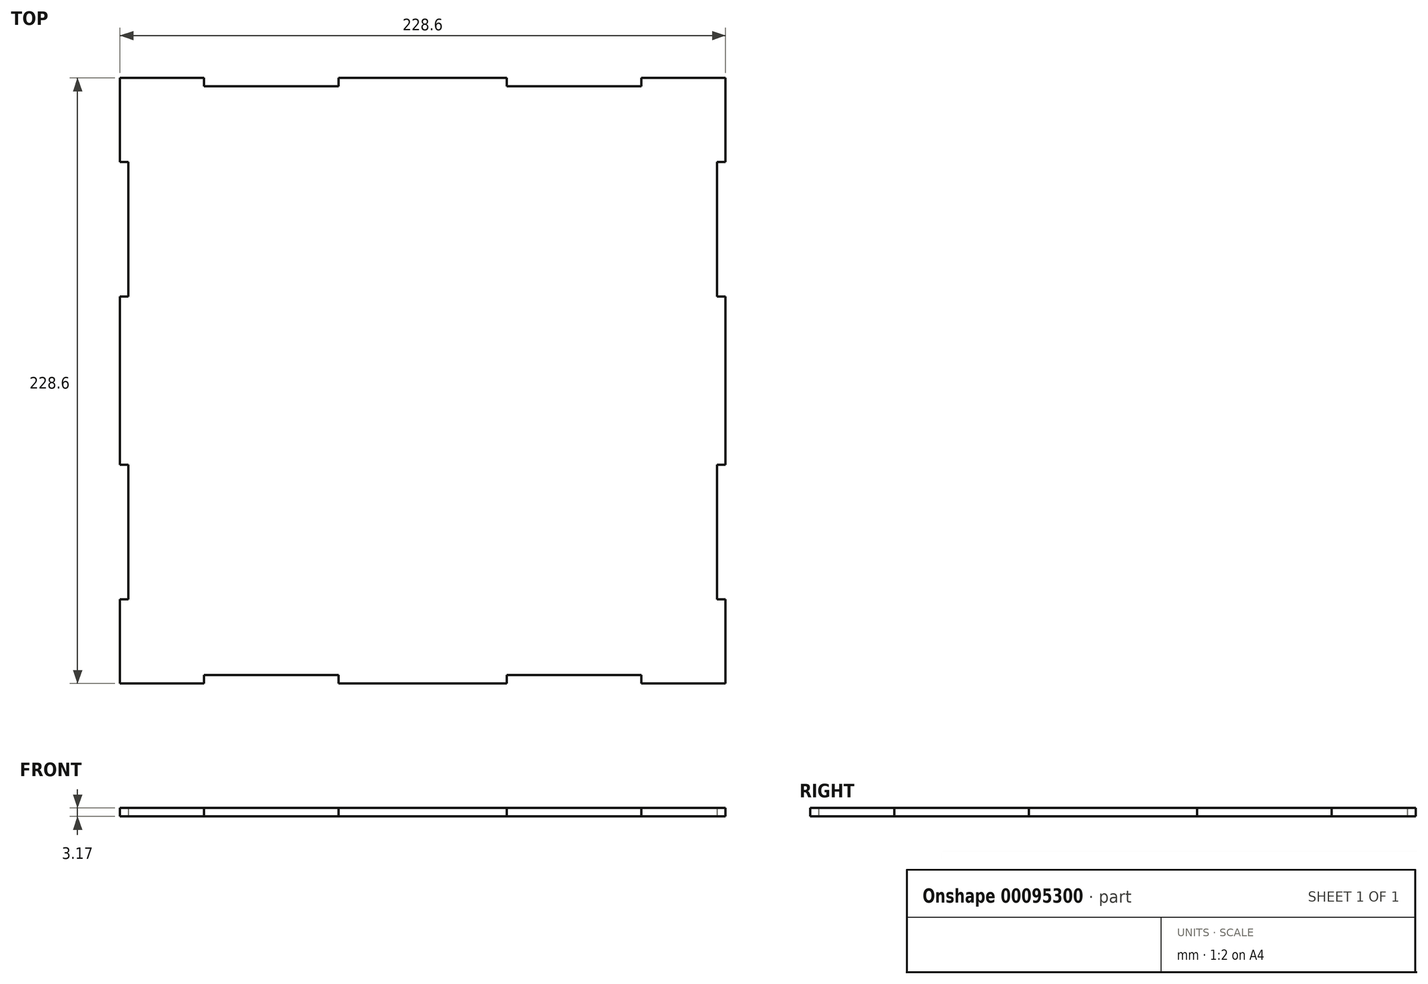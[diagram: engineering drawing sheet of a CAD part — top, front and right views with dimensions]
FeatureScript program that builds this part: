
annotation { "Feature Type Name" : "Feature", "Feature Type Description" : "" }
export const myFeature = defineFeature(function(context is Context, id is Id, definition is map)
    precondition{}
    {
        {
            var Q0;
            Q0=qCreatedBy(makeId("Top.planeOp"),FACE);
            var sketch = newSketch(context, id + "F0", { "sketchPlane" : qUnion([Q0])});
            skLineSegment(sketch, "E0.bottom", {"start": v(114.3, 114.3) * mm, "end": v(-114.3, 114.3) * mm});
            skLineSegment(sketch, "E0.top", {"start": v(114.3, -114.3) * mm, "end": v(-114.3, -114.3) * mm});
            skLineSegment(sketch, "E0.left", {"start": v(114.3, 114.3) * mm, "end": v(114.3, -114.3) * mm});
            skLineSegment(sketch, "E0.right", {"start": v(-114.3, 114.3) * mm, "end": v(-114.3, -114.3) * mm});
            skPoint(sketch, "E0.middle", {"position": v(0, 0) * mm});
            skLineSegment(sketch, "E1.bottom", {"start": v(114.3, 82.55) * mm, "end": v(111.13, 82.55) * mm});
            skLineSegment(sketch, "E1.top", {"start": v(114.3, 31.75) * mm, "end": v(111.13, 31.75) * mm});
            skLineSegment(sketch, "E1.left", {"start": v(114.3, 82.55) * mm, "end": v(114.3, 31.75) * mm});
            skLineSegment(sketch, "E1.right", {"start": v(111.13, 82.55) * mm, "end": v(111.13, 31.75) * mm});
            skLineSegment(sketch, "E2.bottom", {"start": v(114.3, -82.55) * mm, "end": v(111.13, -82.55) * mm});
            skLineSegment(sketch, "E2.top", {"start": v(114.3, -31.75) * mm, "end": v(111.13, -31.75) * mm});
            skLineSegment(sketch, "E2.left", {"start": v(114.3, -82.55) * mm, "end": v(114.3, -31.75) * mm});
            skLineSegment(sketch, "E2.right", {"start": v(111.13, -82.55) * mm, "end": v(111.13, -31.75) * mm});
            skLineSegment(sketch, "E3.bottom", {"start": v(-114.3, 82.55) * mm, "end": v(-111.13, 82.55) * mm});
            skLineSegment(sketch, "E3.top", {"start": v(-114.3, 31.75) * mm, "end": v(-111.13, 31.75) * mm});
            skLineSegment(sketch, "E3.left", {"start": v(-114.3, 82.55) * mm, "end": v(-114.3, 31.75) * mm});
            skLineSegment(sketch, "E3.right", {"start": v(-111.13, 82.55) * mm, "end": v(-111.13, 31.75) * mm});
            skLineSegment(sketch, "E4.bottom", {"start": v(-114.3, -31.75) * mm, "end": v(-111.13, -31.75) * mm});
            skLineSegment(sketch, "E4.top", {"start": v(-114.3, -82.55) * mm, "end": v(-111.13, -82.55) * mm});
            skLineSegment(sketch, "E4.left", {"start": v(-114.3, -31.75) * mm, "end": v(-114.3, -82.55) * mm});
            skLineSegment(sketch, "E4.right", {"start": v(-111.13, -31.75) * mm, "end": v(-111.13, -82.55) * mm});
            skLineSegment(sketch, "E5.bottom", {"start": v(-82.55, -114.3) * mm, "end": v(-31.75, -114.3) * mm});
            skLineSegment(sketch, "E5.top", {"start": v(-82.55, -111.13) * mm, "end": v(-31.75, -111.13) * mm});
            skLineSegment(sketch, "E5.left", {"start": v(-82.55, -114.3) * mm, "end": v(-82.55, -111.13) * mm});
            skLineSegment(sketch, "E5.right", {"start": v(-31.75, -114.3) * mm, "end": v(-31.75, -111.13) * mm});
            skLineSegment(sketch, "E6.bottom", {"start": v(82.55, -114.3) * mm, "end": v(31.75, -114.3) * mm});
            skLineSegment(sketch, "E6.top", {"start": v(82.55, -111.13) * mm, "end": v(31.75, -111.13) * mm});
            skLineSegment(sketch, "E6.left", {"start": v(82.55, -114.3) * mm, "end": v(82.55, -111.13) * mm});
            skLineSegment(sketch, "E6.right", {"start": v(31.75, -114.3) * mm, "end": v(31.75, -111.13) * mm});
            skLineSegment(sketch, "E7.bottom", {"start": v(-82.55, 114.3) * mm, "end": v(-31.75, 114.3) * mm});
            skLineSegment(sketch, "E7.top", {"start": v(-82.55, 111.12) * mm, "end": v(-31.75, 111.12) * mm});
            skLineSegment(sketch, "E7.left", {"start": v(-82.55, 114.3) * mm, "end": v(-82.55, 111.12) * mm});
            skLineSegment(sketch, "E7.right", {"start": v(-31.75, 114.3) * mm, "end": v(-31.75, 111.12) * mm});
            skLineSegment(sketch, "E8.bottom", {"start": v(82.55, 114.3) * mm, "end": v(31.75, 114.3) * mm});
            skLineSegment(sketch, "E8.top", {"start": v(82.55, 111.12) * mm, "end": v(31.75, 111.12) * mm});
            skLineSegment(sketch, "E8.left", {"start": v(82.55, 114.3) * mm, "end": v(82.55, 111.12) * mm});
            skLineSegment(sketch, "E8.right", {"start": v(31.75, 114.3) * mm, "end": v(31.75, 111.12) * mm});
            skSolve(sketch);
        }
        {
            var Q0;
            {var subQ1=sQuery(id+"F0.wireOp",EDGE,"E0.bottom");Q0=makeQuery(id+"F0.imprint","IMPRINT",FACE,{"disambiguationData":[TD([[makeQuery(id+"F0.imprint","IMPRINT",EDGE,{"derivedFrom":subQ1}),1.0]])]});}
            extrude(context, id + "F1", {"entities" : qUnion([Q0]), "depth" : 3.17 * mm});
        }
    });
